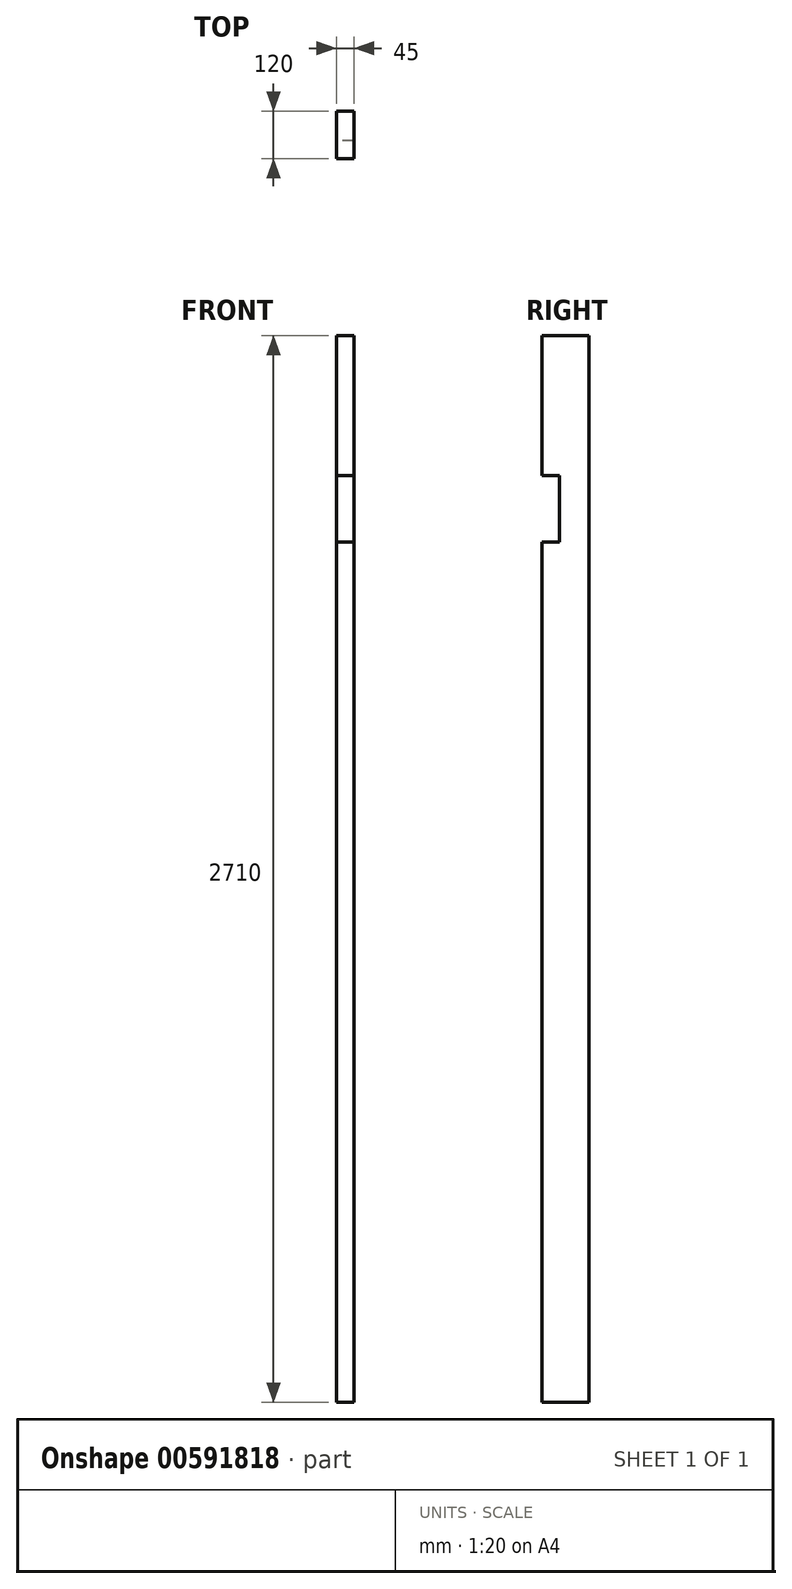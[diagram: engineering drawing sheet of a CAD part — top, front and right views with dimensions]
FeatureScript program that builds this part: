
annotation { "Feature Type Name" : "Feature", "Feature Type Description" : "" }
export const myFeature = defineFeature(function(context is Context, id is Id, definition is map)
    precondition{}
    {
        {
            var Q0;
            Q0=qCreatedBy(makeId("Right.planeOp"),FACE);
            var sketch = newSketch(context, id + "F0", { "sketchPlane" : qUnion([Q0])});
            skLineSegment(sketch, "E0.bottom", {"start": v(0, 0) * mm, "end": v(-120, 0) * mm});
            skLineSegment(sketch, "E0.left", {"start": v(0, 0) * mm, "end": v(0, 2710) * mm});
            skLineSegment(sketch, "E0.right", {"start": v(-120, 0) * mm, "end": v(-120, 2185) * mm});
            skLineSegment(sketch, "E1.bottom", {"start": v(-120, 2355) * mm, "end": v(-75, 2355) * mm});
            skLineSegment(sketch, "E1.top", {"start": v(-120, 2185) * mm, "end": v(-75, 2185) * mm});
            skLineSegment(sketch, "E1.right", {"start": v(-75, 2355) * mm, "end": v(-75, 2185) * mm});
            skPoint(sketch, "E2.end.orphan", {"position": v(-120, 2710) * mm});
            skLineSegment(sketch, "E3", {"start": v(0, 2710) * mm, "end": v(-120, 2710) * mm});
            skLineSegment(sketch, "E4", {"start": v(-120, 2355) * mm, "end": v(-120, 2710) * mm});
            skSolve(sketch);
        }
        {
            var Q0;
            Q0=makeQuery(id+"F0.imprint","IMPRINT",FACE,{"disambiguationData":[TD([[makeQuery(id+"F0.imprint","IMPRINT",EDGE,{"derivedFrom":sQuery(id+"F0.wireOp",EDGE,"E0.bottom")}),-1.0]])]});
            extrude(context, id + "F1", {"entities" : qUnion([Q0]), "depth" : 45 * mm, "offsetDistance" : 25 * mm});
        }
    });
